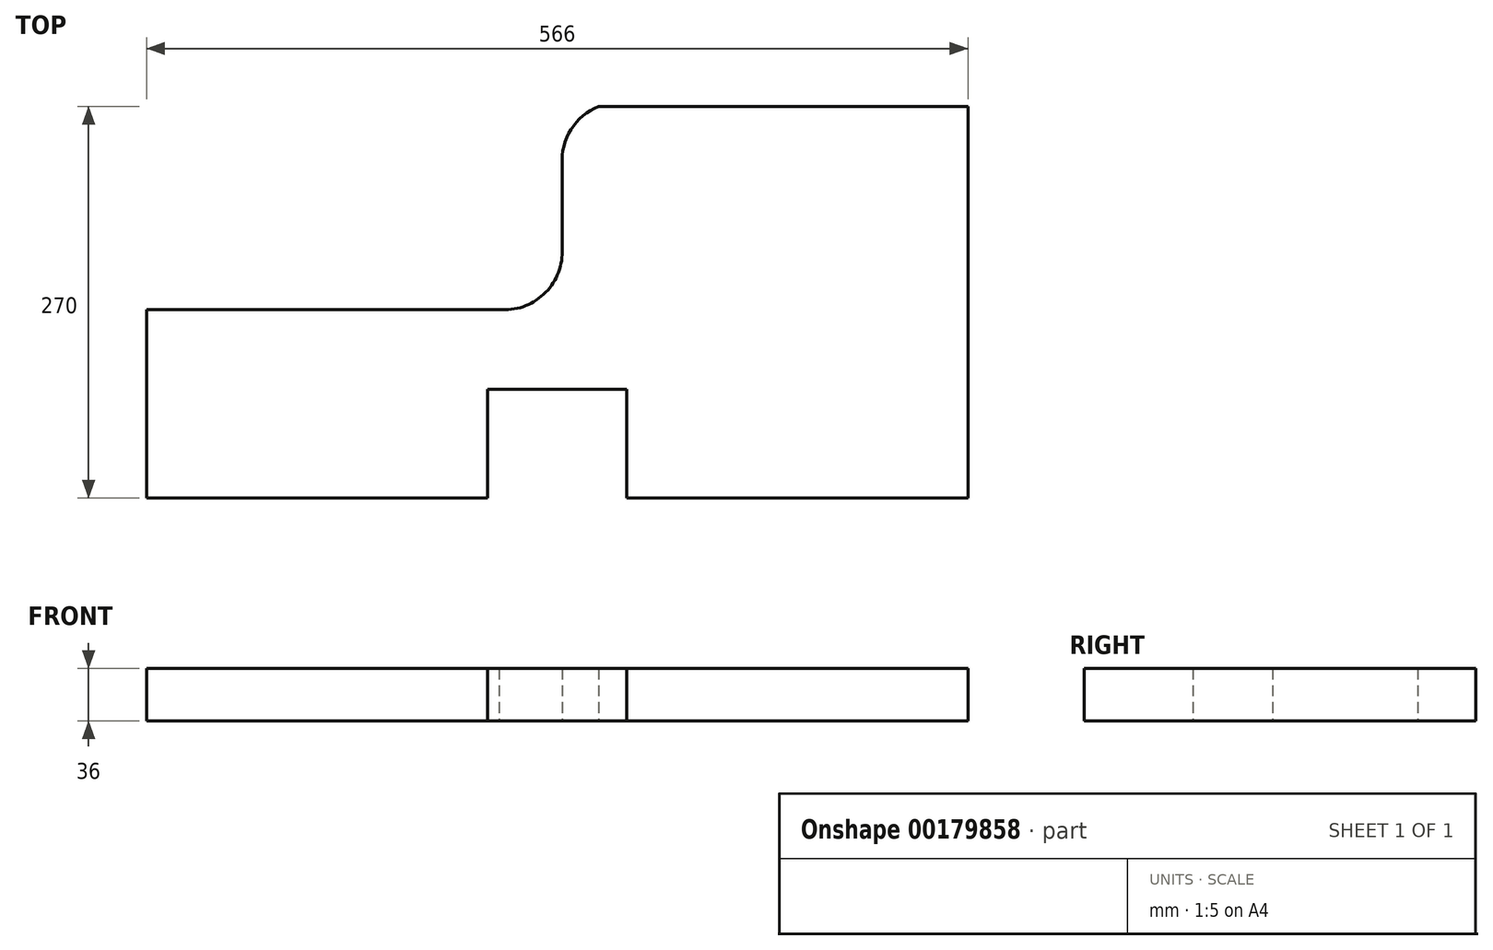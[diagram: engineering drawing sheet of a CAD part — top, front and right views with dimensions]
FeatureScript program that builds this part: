
annotation { "Feature Type Name" : "Feature", "Feature Type Description" : "" }
export const myFeature = defineFeature(function(context is Context, id is Id, definition is map)
    precondition{}
    {
        {
            var Q0;
            Q0=qCreatedBy(makeId("Top.planeOp"),FACE);
            var sketch = newSketch(context, id + "F0", { "sketchPlane" : qUnion([Q0])});
            skLineSegment(sketch, "E0", {"start": v(-288.39, -152.46) * mm, "end": v(-288.39, -22.46) * mm});
            skLineSegment(sketch, "E1", {"start": v(277.61, 117.54) * mm, "end": v(277.61, -152.46) * mm});
            skLineSegment(sketch, "E2", {"start": v(277.61, -152.46) * mm, "end": v(-288.39, -152.46) * mm});
            skLineSegment(sketch, "E3", {"start": v(-45.39, -47.62) * mm, "end": v(-45.39, 142.6) * mm, "construction": true});
            skLineSegment(sketch, "E4", {"start": v(-45.39, 17.54) * mm, "end": v(19.73, 17.54) * mm, "construction": true});
            skArc(sketch, "E5", {"start": v(-45.39, -22.46) * mm, "mid": v(-14.86, -12.03) * mm, "end": v(-1.97, 17.54) * mm});
            skLineSegment(sketch, "E6", {"start": v(-1.97, 77.54) * mm, "end": v(23.2, 77.54) * mm, "construction": true});
            skLineSegment(sketch, "E7", {"start": v(23.2, 77.54) * mm, "end": v(23.2, 117.54) * mm, "construction": true});
            skArc(sketch, "E8", {"start": v(23.2, 117.54) * mm, "mid": v(4.08, 101.65) * mm, "end": v(-1.97, 77.54) * mm});
            skLineSegment(sketch, "E9", {"start": v(-288.39, -22.46) * mm, "end": v(-45.39, -22.46) * mm});
            skLineSegment(sketch, "E10", {"start": v(-1.97, 17.54) * mm, "end": v(-1.97, 77.54) * mm});
            skLineSegment(sketch, "E11", {"start": v(23.2, 117.54) * mm, "end": v(277.61, 117.54) * mm});
            skLineSegment(sketch, "E12", {"start": v(-53.39, -152.46) * mm, "end": v(-53.39, -77.46) * mm});
            skLineSegment(sketch, "E13", {"start": v(-53.39, -77.46) * mm, "end": v(42.61, -77.46) * mm});
            skLineSegment(sketch, "E14", {"start": v(42.61, -77.46) * mm, "end": v(42.61, -152.46) * mm});
            skLineSegment(sketch, "E15", {"start": v(42.61, -152.46) * mm, "end": v(-53.39, -152.46) * mm});
            skLineSegment(sketch, "E16", {"start": v(-5.39, -77.46) * mm, "end": v(-5.39, -152.46) * mm, "construction": true});
            skLineSegment(sketch, "E17", {"start": v(-5.39, -77.46) * mm, "end": v(-5.39, 135.35) * mm, "construction": true});
            skSolve(sketch);
        }
        {
            var Q0;
            Q0=makeQuery(id+"F0.imprint","IMPRINT",FACE,{"disambiguationData":[TD([[makeQuery(id+"F0.imprint","IMPRINT",EDGE,{"derivedFrom":sQuery(id+"F0.wireOp",EDGE,"E0")}),-1.0]])]});
            extrude(context, id + "F1", {"entities" : qUnion([Q0]), "depth" : 36 * mm});
        }
    });
